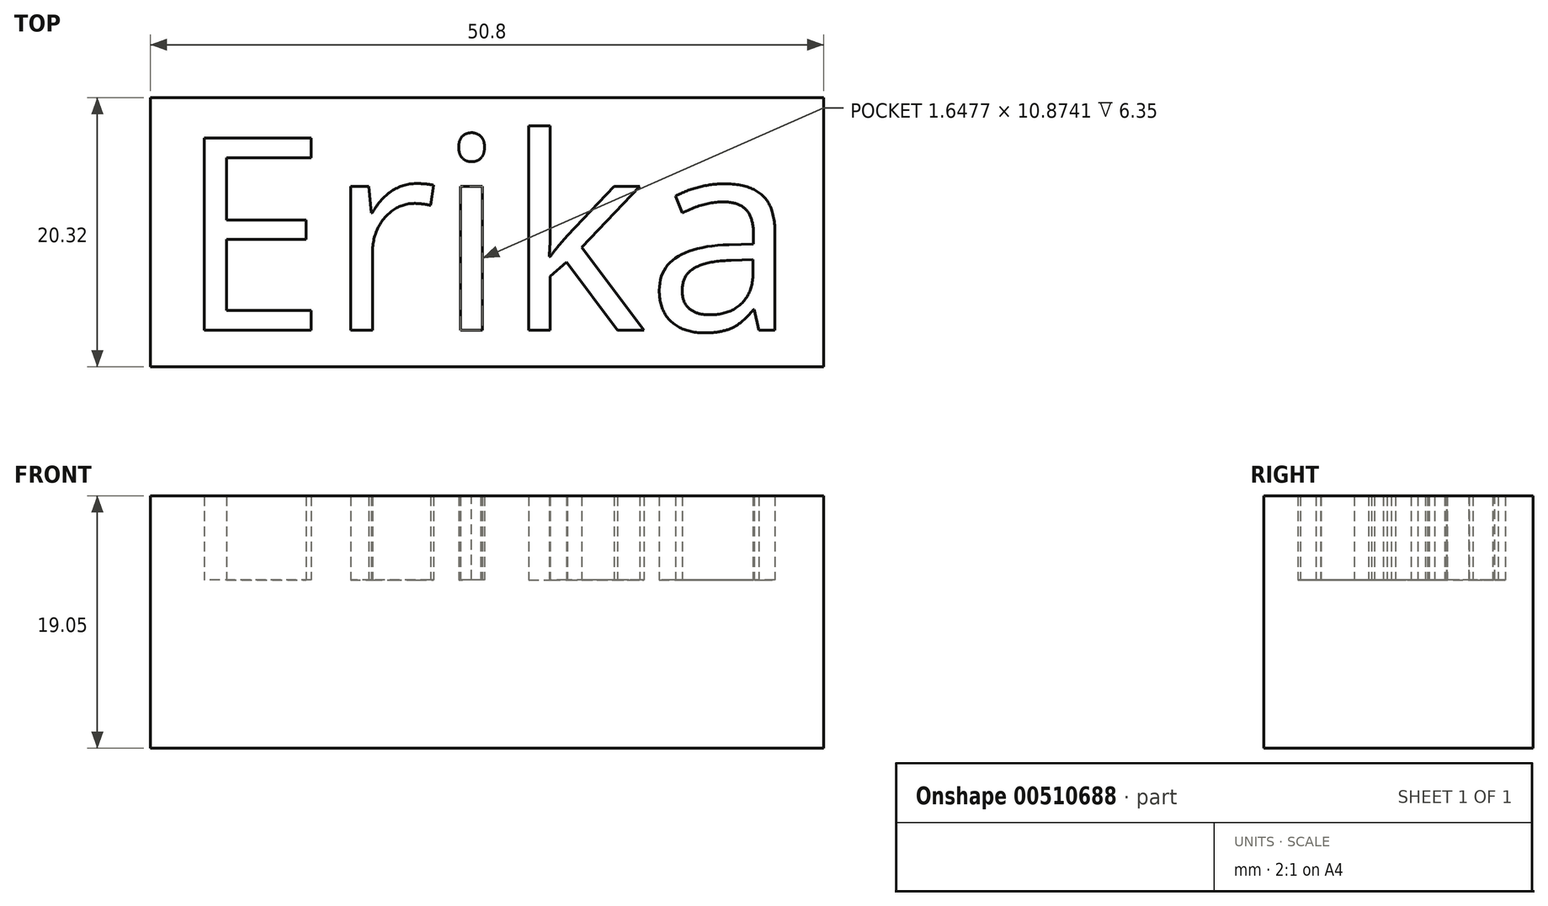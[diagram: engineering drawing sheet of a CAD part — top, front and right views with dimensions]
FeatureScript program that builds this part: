
annotation { "Feature Type Name" : "Feature", "Feature Type Description" : "" }
export const myFeature = defineFeature(function(context is Context, id is Id, definition is map)
    precondition{}
    {
        {
            var Q0;
            Q0=qCreatedBy(makeId("Top.planeOp"),FACE);
            var sketch = newSketch(context, id + "F0", { "sketchPlane" : qUnion([Q0])});
            skLineSegment(sketch, "E0.bottom", {"start": v(-21.26, 17.56) * mm, "end": v(29.54, 17.56) * mm});
            skLineSegment(sketch, "E0.top", {"start": v(-21.26, -2.76) * mm, "end": v(29.54, -2.76) * mm});
            skLineSegment(sketch, "E0.left", {"start": v(-21.26, 17.56) * mm, "end": v(-21.26, -2.76) * mm});
            skLineSegment(sketch, "E0.right", {"start": v(29.54, 17.56) * mm, "end": v(29.54, -2.76) * mm});
            skText(sketch, "E1", { "text": "Erika", "fontName": "OpenSans-Regular.ttf"});
            skFitSpline(sketch, "E2", {"points": [v(-21.26, 17.56) * mm, v(-29.93, 12.77) * mm, v(-35.49, 17.56) * mm, v(-44.12, 9.7) * mm, v(-35.22, 0) * mm, v(-28.1, 4.42) * mm, v(-21.26, -2.76) * mm], "startDerivative": vector(-46.47, -43.58) * mm, "endDerivative": vector(35.15, -83.95) * mm});
            const initialGuessF0  = {"E1": [-0.0192, 0, 1, 0, 0.01463]};
            skSetInitialGuess(sketch, initialGuessF0);
            skSolve(sketch);
        }
        {
            var Q0;
            Q0=makeQuery(id+"F0.imprint","IMPRINT",FACE,{"disambiguationData":[TD([[makeQuery(id+"F0.imprint","IMPRINT",EDGE,{"derivedFrom":sQuery(id+"F0.wireOp",EDGE,"E1.sketch_text.stroke-0")}),-1.0]])]});
            var Q1;
            Q1=makeQuery(id+"F0.imprint","IMPRINT",FACE,{"disambiguationData":[TD([[makeQuery(id+"F0.imprint","IMPRINT",EDGE,{"derivedFrom":sQuery(id+"F0.wireOp",EDGE,"E1.sketch_text.stroke-12")}),-1.0]])]});
            var Q2;
            Q2=makeQuery(id+"F0.imprint","IMPRINT",FACE,{"disambiguationData":[TD([[makeQuery(id+"F0.imprint","IMPRINT",EDGE,{"derivedFrom":sQuery(id+"F0.wireOp",EDGE,"E1.sketch_text.stroke-25")}),-1.0]])]});
            var Q3;
            Q3=makeQuery(id+"F0.imprint","IMPRINT",FACE,{"disambiguationData":[TD([[makeQuery(id+"F0.imprint","IMPRINT",EDGE,{"derivedFrom":sQuery(id+"F0.wireOp",EDGE,"E1.sketch_text.stroke-29")}),-1.0]])]});
            var Q4;
            Q4=makeQuery(id+"F0.imprint","IMPRINT",FACE,{"disambiguationData":[TD([[makeQuery(id+"F0.imprint","IMPRINT",EDGE,{"derivedFrom":sQuery(id+"F0.wireOp",EDGE,"E1.sketch_text.stroke-37")}),-1.0]])]});
            var Q5;
            Q5=makeQuery(id+"F0.imprint","IMPRINT",FACE,{"disambiguationData":[TD([[makeQuery(id+"F0.imprint","IMPRINT",EDGE,{"derivedFrom":sQuery(id+"F0.wireOp",EDGE,"E1.sketch_text.stroke-52")}),-1.0]])]});
            extrude(context, id + "F1", {"entities" : qUnion([Q0, Q1, Q2, Q3, Q4, Q5]), "depth" : 12.7 * mm});
        }
        {
            var Q0;
            Q0=makeQuery(id+"F0.imprint","IMPRINT",FACE,{"disambiguationData":[TD([[makeQuery(id+"F0.imprint","IMPRINT",EDGE,{"derivedFrom":sQuery(id+"F0.wireOp",EDGE,"E0.bottom")}),-1.0]])]});
            var Q1;
            Q1=makeQuery(id+"F0.imprint","IMPRINT",FACE,{"disambiguationData":[TD([[makeQuery(id+"F0.imprint","IMPRINT",EDGE,{"derivedFrom":sQuery(id+"F0.wireOp",EDGE,"E1.sketch_text.stroke-71")}),1.0]])]});
            extrude(context, id + "F2", {"entities" : qUnion([Q0, Q1]), "operationType" : NewBodyOperationType.ADD, "depth" : 19.05 * mm});
        }
    });
